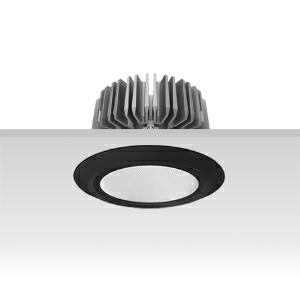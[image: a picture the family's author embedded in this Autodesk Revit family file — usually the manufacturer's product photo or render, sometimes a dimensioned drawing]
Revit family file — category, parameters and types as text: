
# Revit family: 3f_filippi_-_3f_reno_bianco_ampio_3f_filippi_-_30358_a01036_-_3f_reno_150_wh_2000-840_ep_wide___vs_bk_fa1f
name_source: partatom
category: Lighting Fixtures
units: mm (PartAtom-declared; Revit-internal decimal feet)

## family parameters
Cut with Voids When Loaded = No
Host = Face
Light Source = No
Part Type = Normal
Room Calculation Point = No
Round Connector Dimension = Use Diameter
Shared = No

## types (1)
- 3F Filippi - 3F Reno Bianco Ampio (1 x LED, 1709 lm, 21 W, 4000 K)
    Apparent Load = 21 VA
    Approval mark = ENEC
    CIE Flux Codes = 74 93 99 100 100
    Color Rendering = 80
    Color Temperature = 4000 K
    Control Gear = Electronic ballast
    Default Elevation = 1800 mm
    Description = ILLUMINOTECHNICAL
Luminous efficiency 100% (DLOR 100%, ULOR 0%).
Initial luminous flux of the luminaire 1709 lm.
Emergency luminaire luminous flux BLF 20%.
Direct symmetric wide distribution.
Installation Interdistance Transv.D = 1.12 x hu - Long.D = 1.11 x hu.
Tabular UGR (CIE 117 - 4H-8H; S=0.25H; 70/50/20): RUG 22.8 - 22.7.
Beam angle: 74° - 73°.
Luminous efficacy 81 lm/W.
Lifetime (L90/B10): 30000 h. (tq+25°C)
Lifetime (L85/B10): 50000 h. (tq+25°C)
Lifetime (L70/B10): 80000 h. (tq+25°C)
Sudden decreased luminous flux after 50000 hours: 0% (C0).
Photobiological safety in compliance with IEC/TR 62778: RG0 risk exempt, (IEC 62471).
In compliance with IEC/EN 62722-2-1 - IEC/EN 62717 standards.

SOURCE
Compact LED module 2000/840.
Energy efficiency class (UE 2019/2020 - UE 2019/2015): D.
CIE 13.3 Colour rendering index: CRI >80 (R9 <50%).
IES TM-30 Fidelity Index: Rf = 84 Rg = 95.
CCT nominal colour temperature 4000 K.
Colour initial tolerance (MacAdam): SDCM 3.
Zhaga Book 3 compliant.

MECHANICAL
Passive heat dissipator in die-casting aluminium, oversized, for optimum thermal management of the LED module.
Parabolic element with graduated/concentric rings in white polycarbonate.
Transparent external lens with glossy and satin differentiated surfaces, with a cooling and anti-insect system in methacrylate (PMMA).
Fastening spring clips in stainless steel.
Dimensions: diameter 176 mm, height 111 mm. Weight 1.3 kg.
IP44 protection degree for exposed part, IP20 for recessed part.
Mechanical strength to impacts IK06 (1 joule).
Glow-wire test resistance 650°C.

ELECTRICAL
Wiring on a separate unit.
Halogen Free electronic wiring 230V-50/60Hz, power factor 0.90, THD <25%, constant output current, SELV, class II, 1 driver.
Power of the luminaire 21 W.
CE - IEC 60598-1 - EN 60598-1.
EP maintained emergency wiring on board, 1h duration, 24h recharge; compliant with EN 60598-2-22, excluding high risk areas.
SAFE FLICKER: PstLM=<1 and SVM=<0.4 (IEC TR 61547-1 and IEC TR 63158), to ensure a more comfortable and safe light.
Ambient temperature from +5°C to +25°C.
Temperature class T6 max 85°C.
Relative humidity UR: <85%.

INSTALLATION
Pull-up recessed fitting.
False ceiling carving: 150 mm.
All accessories dedicated to this product are available on the Catalog and on our website www.3F-Filippi.com.

ACCESSORIES
A01036 - Anti-glare microprismatic VS moulded glass, tempered, not flammable, locked and in line with the trim, in black polycarbonate.

APPLICATIONS
Environments: architectural, commercial, exhibition areas, transit areas, corridors, shops, display windows, service areas.
In false ceilings with narrow voids.

WARNING
Luminaire designed for disposal/recycling at end-of-life.
Replaceable (LED only) light source by a professional. Replaceable control gear by a professional.
    Height = 0 mm  [stored 0 ft]
    Lamp = 1 x LED
    Lamp Light Flux = 1709 lm
    Lamp Power = 21 W
    Lamp count = 1
    Length = 176 mm
    Lifetime = 50000 h
    Luminous efficacy = 81 lm/W
    Manufacturer = 3F Filippi
    ModVariant = No
    Model = 3F Filippi - 30358+A01036 - 3F Reno 150 WH 2000-840 EP WIDE + VS BK
    Mounting Place = Ceiling
    Mounting Type = Recessed
    Number of Poles = 1
    OnlyDefault = Yes
    Power Factor = 1
    Product Name = 3F Filippi - 3F Reno Bianco Ampio
    Product group = recessed luminaire
    ProductGroupID = 4
    Protection Class = Protection class II
    Protection Degree = IP 20
    RLX_Detail_Level = 1
    RLX_Emergency_Light_Flux = 0 lm
    RLX_Emergency_Type = 0
    RLX_Emergency_Type_DB = No
    RlxData = <blob elided: 84977 chars, md5=0da525d1>
    Socket = socket
    Standby Power = 0 W
    System Light Flux = 1709 lm
    System Power = 21 W
    Type Comments = Product without accessories
    Type Image = 3ffilippi_3f_reno_150_bk_vs_smp.jpg
    URL = http://relux.com
    VarID = ---
    Voltage = 0 V
    Weight = 0.00 kg
    Width = 0 mm  [stored 0 ft]

note: [stored X ft] marks values corroborated as IEEE doubles in the binary element streams (Revit-internal decimal feet)

## geometry (parser evidence)
native form markers: Blend x4, Sweep x11
no freeform markers — native parametric forms only
